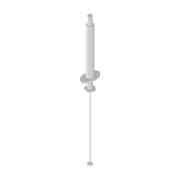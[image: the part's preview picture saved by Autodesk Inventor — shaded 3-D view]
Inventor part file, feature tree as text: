
AUTODESK INVENTOR PART (.ipt)
format: ipt  version: 2022 (Build 260153000, 153)  size: 117,760 bytes
history: native  units: mm
features: extrude x7, sketch x7
ambient origin geometry x8: Origin, YZ Plane, XZ Plane, XY Plane, X Axis, Y Axis, Z Axis, Center Point
bodies: Volumenkörper1 (feature_tree)
feature tree (14):
  extrude  "Extrusion1"  Depth=47.6mm TaperAngle=0.0deg
  extrude  "Extrusion2"  Depth=8.5mm TaperAngle=0.0deg
  extrude  "Extrusion3"  Depth=9.5mm
  extrude  "Extrusion4"  Depth=1.5mm
  extrude  "Extrusion5"  Depth=9.5mm
  extrude  "Extrusion6"  Depth=1.2mm
  extrude  "Extrusion7"  Depth=1.2mm TaperAngle=0.0deg
  sketch  "Skizze1"  dims[d0=6.44mm d1=47.6mm d2=0.0mm]
  sketch  "Skizze2"  dims[d3=4.1mm d4=8.5mm d5=0.0mm]
  sketch  "Skizze3"  dims[d6=9.5mm d7=5.25mm]
  sketch  "Skizze4"  dims[d8=1.5mm d9=0.0mm d10=4.33mm]
  sketch  "Skizze5"  dims[d11=9.5mm d12=0.0mm d13=8.6mm]
  sketch  "Skizze6"  dims[d14=1.2mm d15=0.0mm d16=1.0mm]
  sketch  "Skizze7"  dims[d17=68.2mm d18=0.0mm d19=1.2mm d20=0.0mm]
